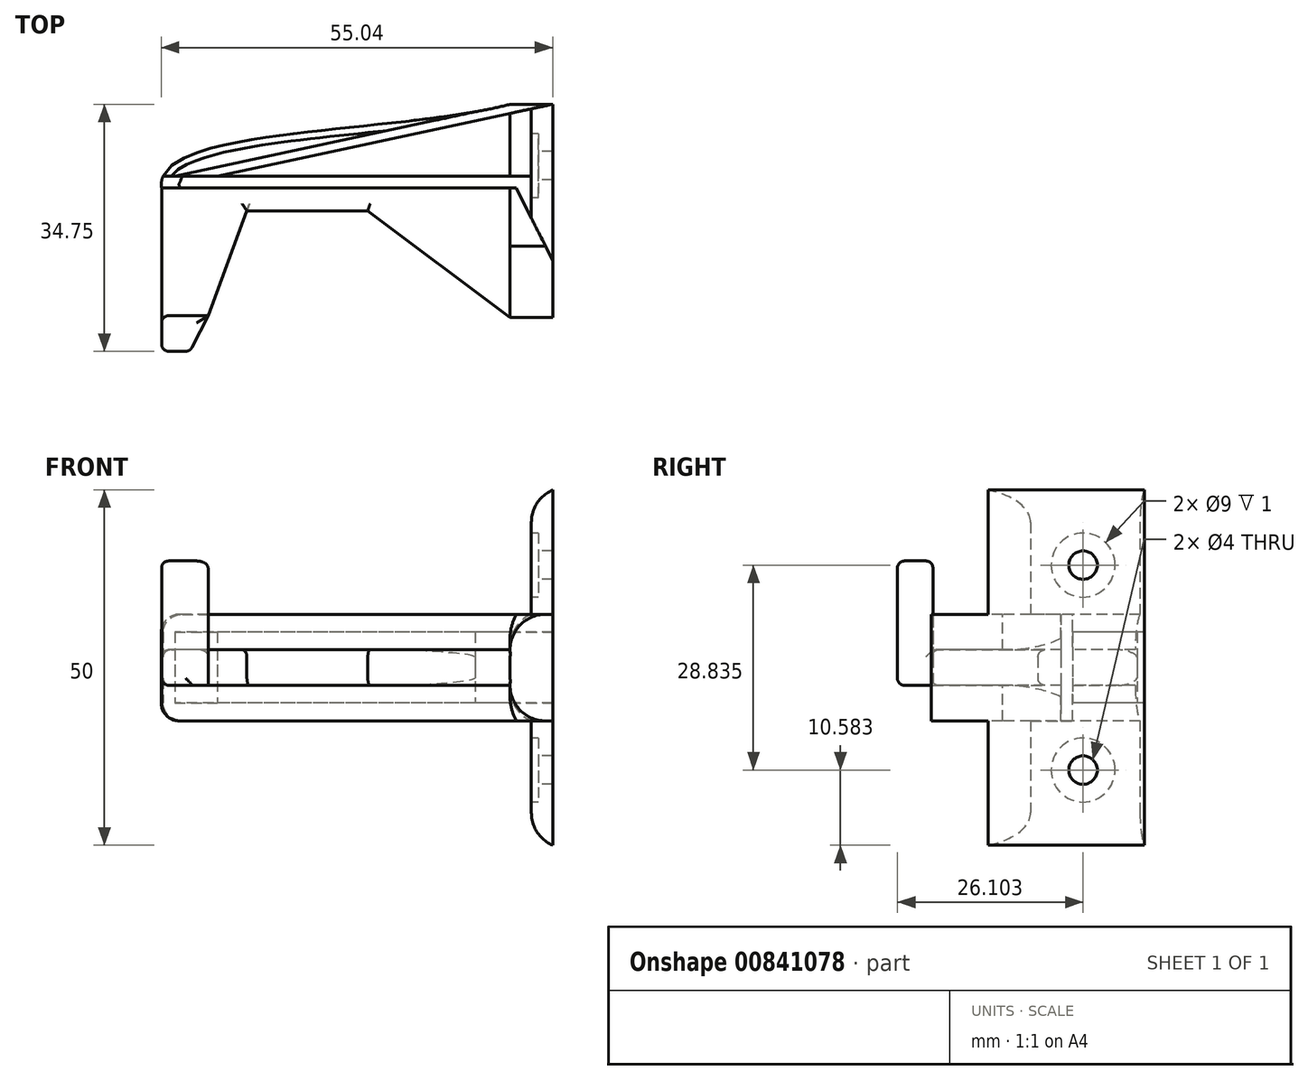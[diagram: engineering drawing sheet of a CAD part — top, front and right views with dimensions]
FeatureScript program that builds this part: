
annotation { "Feature Type Name" : "Feature", "Feature Type Description" : "" }
export const myFeature = defineFeature(function(context is Context, id is Id, definition is map)
    precondition{}
    {
        {
            var Q0;
            Q0=qCreatedBy(makeId("Top.planeOp"),FACE);
            var sketch = newSketch(context, id + "F0", { "sketchPlane" : qUnion([Q0])});
            skLineSegment(sketch, "E0.bottom", {"start": v(24.18, 10.1) * mm, "end": v(30.18, 10.1) * mm});
            skLineSegment(sketch, "E0.top", {"start": v(24.18, -19.9) * mm, "end": v(30.18, -19.9) * mm});
            skLineSegment(sketch, "E0.left", {"start": v(24.18, 10.1) * mm, "end": v(24.18, -19.9) * mm});
            skLineSegment(sketch, "E0.right", {"start": v(30.18, 10.1) * mm, "end": v(30.18, -19.9) * mm});
            skLineSegment(sketch, "E1.right", {"start": v(-18.28, -1.64) * mm, "end": v(-18.28, -4.87) * mm});
            skLineSegment(sketch, "E2.bottom", {"start": v(-18.28, -1.64) * mm, "end": v(-24.82, -1.64) * mm});
            skLineSegment(sketch, "E2.right", {"start": v(-24.82, -1.64) * mm, "end": v(-24.82, -24.64) * mm});
            skLineSegment(sketch, "E3", {"start": v(-24.82, -19.64) * mm, "end": v(-18.28, -19.64) * mm});
            skLineSegment(sketch, "E4", {"start": v(27.18, 10.1) * mm, "end": v(27.18, -19.9) * mm});
            skLineSegment(sketch, "E5", {"start": v(-24.82, -24.64) * mm, "end": v(-20.82, -24.64) * mm});
            skLineSegment(sketch, "E6", {"start": v(-20.82, -24.64) * mm, "end": v(-18.28, -19.64) * mm});
            skLineSegment(sketch, "E7", {"start": v(-18.28, -4.87) * mm, "end": v(-18.28, -19.64) * mm});
            skLineSegment(sketch, "E8", {"start": v(4.18, -4.87) * mm, "end": v(24.18, -19.9) * mm});
            skLineSegment(sketch, "E9", {"start": v(27.18, -5.9) * mm, "end": v(30.18, -11.87) * mm});
            skLineSegment(sketch, "E10", {"start": v(-18.28, -4.87) * mm, "end": v(4.18, -4.87) * mm});
            skFitSpline(sketch, "E11", {"points": [v(24.18, 10.1) * mm, v(-24.82, -1.64) * mm], "startDerivative": vector(-47.95, -12.64) * mm, "endDerivative": vector(4, -26.04) * mm});
            skLineSegment(sketch, "E12", {"start": v(-18.28, -19.64) * mm, "end": v(-12.82, -4.87) * mm});
            skLineSegment(sketch, "E13", {"start": v(-18.28, -1.64) * mm, "end": v(30.18, -1.64) * mm});
            skLineSegment(sketch, "E14", {"start": v(-24.61, 0) * mm, "end": v(30.18, 0) * mm});
            skLineSegment(sketch, "E15", {"start": v(30.18, 10.1) * mm, "end": v(-16.96, 0) * mm});
            skLineSegment(sketch, "E16", {"start": v(24.18, 10.1) * mm, "end": v(-22.96, 0) * mm});
            skSolve(sketch);
        }
        {
            var Q0;
            Q0=makeQuery(id+"F0.imprint","IMPRINT",FACE,{"disambiguationData":[TD([[makeQuery(id+"F0.imprint","IMPRINT",EDGE,{"derivedFrom":sQuery(id+"F0.wireOp",EDGE,"E1.right")}),-1.0]])]});
            var Q1;
            {var subQ2=sQuery(id+"F0.wireOp",EDGE,"E3");Q1=makeQuery(id+"F0.imprint","IMPRINT",FACE,{"disambiguationData":[TD([[makeQuery(id+"F0.imprint","IMPRINT",EDGE,{"derivedFrom":subQ2}),-1.0]])]});}
            var Q2;
            {var subQ2=sQuery(id+"F0.wireOp",EDGE,"E1.right");Q2=makeQuery(id+"F0.imprint","IMPRINT",FACE,{"disambiguationData":[TD([[makeQuery(id+"F0.imprint","IMPRINT",EDGE,{"derivedFrom":subQ2}),1.0]])]});}
            var Q3;
            {var subQ0=sQuery(id+"F0.wireOp",EDGE,"E15");var subQ1=sQuery(id+"F0.wireOp",EDGE,"E0.left");var subQ2=makeQuery(id+"F0.imprint","INTERSECT",VERTEX,{"derivedFrom":[subQ1,subQ0]});Q3=makeQuery(id+"F0.imprint","IMPRINT",FACE,{"disambiguationData":[TD([[makeQuery(id+"F0.imprint","IMPRINT",EDGE,{"disambiguationData":[TD([[subQ2,-1.0]])],"derivedFrom":subQ1}),-1.0]])]});}
            var Q4;
            {var subQ0=sQuery(id+"F0.wireOp",EDGE,"E11");var subQ5=sQuery(id+"F0.wireOp",EDGE,"E14");var subQ6=makeQuery(id+"F0.imprint","INTERSECT",VERTEX,{"derivedFrom":[subQ0,subQ5]});Q4=makeQuery(id+"F0.imprint","IMPRINT",FACE,{"disambiguationData":[TD([[makeQuery(id+"F0.imprint","IMPRINT",EDGE,{"disambiguationData":[TD([[subQ6,-1.0]])],"derivedFrom":subQ5}),1.0]])]});}
            var Q5;
            {var subQ0=sQuery(id+"F0.wireOp",EDGE,"E7");Q5=makeQuery(id+"F0.imprint","IMPRINT",FACE,{"disambiguationData":[TD([[makeQuery(id+"F0.imprint","IMPRINT",EDGE,{"derivedFrom":subQ0}),1.0]])]});}
            extrude(context, id + "F1", {"entities" : qUnion([Q0, Q1, Q2, Q3, Q4, Q5]), "endBound" : BoundingType.SYMMETRIC, "depth" : 5 * mm, "offsetDistance" : 25 * mm});
        }
        {
            var Q0;
            {var subQ3=sQuery(id+"F0.wireOp",EDGE,"E1.left");Q0=makeQuery(id+"F0.imprint","IMPRINT",FACE,{"disambiguationData":[TD([[makeQuery(id+"F0.imprint","IMPRINT",EDGE,{"derivedFrom":subQ3}),1.0]])]});}
            var Q1;
            {var subQ5=sQuery(id+"F0.wireOp",EDGE,"E9");Q1=makeQuery(id+"F0.imprint","IMPRINT",FACE,{"disambiguationData":[TD([[makeQuery(id+"F0.imprint","IMPRINT",EDGE,{"derivedFrom":subQ5}),-1.0]])]});}
            var Q2;
            {var subQ0=sQuery(id+"F0.wireOp",EDGE,"E4");var subQ1=makeQuery(id+"F0.imprint","INTERSECT",VERTEX,{"derivedFrom":[subQ0,sQuery(id+"F0.wireOp",EDGE,"E9")]});Q2=makeQuery(id+"F0.imprint","IMPRINT",FACE,{"disambiguationData":[TD([[makeQuery(id+"F0.imprint","IMPRINT",EDGE,{"disambiguationData":[TD([[subQ1,1.0]])],"derivedFrom":subQ0}),-1.0]])]});}
            var Q3;
            {var subQ0=sQuery(id+"F0.wireOp",EDGE,"E14");var subQ1=sQuery(id+"F0.wireOp",EDGE,"E0.left");var subQ2=makeQuery(id+"F0.imprint","INTERSECT",VERTEX,{"derivedFrom":[subQ1,subQ0]});Q3=makeQuery(id+"F0.imprint","IMPRINT",FACE,{"disambiguationData":[TD([[makeQuery(id+"F0.imprint","IMPRINT",EDGE,{"disambiguationData":[TD([[subQ2,-1.0]])],"derivedFrom":subQ1}),1.0]])]});}
            var Q4;
            {var subQ0=sQuery(id+"F0.wireOp",EDGE,"E15");var subQ1=sQuery(id+"F0.wireOp",EDGE,"E0.left");var subQ2=makeQuery(id+"F0.imprint","INTERSECT",VERTEX,{"derivedFrom":[subQ1,subQ0]});Q4=makeQuery(id+"F0.imprint","IMPRINT",FACE,{"disambiguationData":[TD([[makeQuery(id+"F0.imprint","IMPRINT",EDGE,{"disambiguationData":[TD([[subQ2,-1.0]])],"derivedFrom":subQ1}),1.0]])]});}
            var Q5;
            {var subQ1=sQuery(id+"F0.wireOp",EDGE,"E2.bottom");Q5=makeQuery(id+"F0.imprint","IMPRINT",FACE,{"disambiguationData":[TD([[makeQuery(id+"F0.imprint","IMPRINT",EDGE,{"derivedFrom":subQ1}),-1.0]])]});}
            extrude(context, id + "F2", {"entities" : qUnion([Q0, Q1, Q2, Q3, Q4, Q5]), "operationType" : NewBodyOperationType.ADD, "endBound" : BoundingType.SYMMETRIC, "depth" : 15 * mm, "offsetDistance" : 25 * mm});
        }
        {
            var Q0;
            {var subQ5=sQuery(id+"F0.wireOp",EDGE,"E9");Q0=makeQuery(id+"F0.imprint","IMPRINT",FACE,{"disambiguationData":[TD([[makeQuery(id+"F0.imprint","IMPRINT",EDGE,{"derivedFrom":subQ5}),1.0]])]});}
            var Q1;
            {var subQ0=sQuery(id+"F0.wireOp",EDGE,"E15");var subQ5=sQuery(id+"F0.wireOp",EDGE,"E4");var subQ6=makeQuery(id+"F0.imprint","INTERSECT",VERTEX,{"derivedFrom":[subQ5,subQ0]});Q1=makeQuery(id+"F0.imprint","IMPRINT",FACE,{"disambiguationData":[TD([[makeQuery(id+"F0.imprint","IMPRINT",EDGE,{"disambiguationData":[TD([[subQ6,-1.0]])],"derivedFrom":subQ5}),1.0]])]});}
            var Q2;
            {var subQ0=sQuery(id+"F0.wireOp",EDGE,"E13");var subQ1=sQuery(id+"F0.wireOp",EDGE,"E0.right");var subQ2=makeQuery(id+"F0.imprint","INTERSECT",VERTEX,{"derivedFrom":[subQ1,subQ0]});Q2=makeQuery(id+"F0.imprint","IMPRINT",FACE,{"disambiguationData":[TD([[makeQuery(id+"F0.imprint","IMPRINT",EDGE,{"disambiguationData":[TD([[subQ2,1.0]])],"derivedFrom":subQ1}),-1.0]])]});}
            extrude(context, id + "F3", {"entities" : qUnion([Q0, Q1, Q2]), "operationType" : NewBodyOperationType.ADD, "endBound" : BoundingType.SYMMETRIC, "depth" : 50 * mm, "offsetDistance" : 25 * mm});
        }
        {
            var Q0;
            {var subQ2=sQuery(id+"F0.wireOp",EDGE,"E3");Q0=makeQuery(id+"F0.imprint","IMPRINT",FACE,{"disambiguationData":[TD([[makeQuery(id+"F0.imprint","IMPRINT",EDGE,{"derivedFrom":subQ2}),-1.0]])]});}
            var Q1;
            Q1=makeQuery(id+"F1.opExtrude","SWEPT_BODY",BODY,{"disambiguationData":[OSD([sQuery(id+"F0.wireOp",EDGE,"E0.left"),sQuery(id+"F0.wireOp",EDGE,"E1.left"),sQuery(id+"F0.wireOp",EDGE,"E2.right"),sQuery(id+"F0.wireOp",EDGE,"E3"),sQuery(id+"F0.wireOp",EDGE,"E7"),sQuery(id+"F0.wireOp",EDGE,"2QqUce5b-Nnzw-vXuS-maCt-9JAGvlBEQTfu"),sQuery(id+"F0.wireOp",EDGE,"nEMrKmD4-wK41-gVLx-OtnK-8CKE1vO8Bu5v"),sQuery(id+"F0.wireOp",EDGE,"E8"),sQuery(id+"F0.wireOp",EDGE,"b5387394-8ce0-4926-b781-dd25e73307f8")])]});
            extrude(context, id + "F4", {"entities" : qUnion([Q0]), "operationType" : NewBodyOperationType.ADD, "depth" : 15 * mm, "endBoundEntityBody" : qUnion([Q1]), "offsetDistance" : 25 * mm});
        }
        {
            var Q0;
            {var subQ2=sQuery(id+"F0.wireOp",EDGE,"E3");Q0=makeQuery(id+"F0.imprint","IMPRINT",FACE,{"disambiguationData":[TD([[makeQuery(id+"F0.imprint","IMPRINT",EDGE,{"derivedFrom":subQ2}),-1.0]])]});}
            extrude(context, id + "F5", {"entities" : qUnion([Q0]), "operationType" : NewBodyOperationType.ADD, "endBound" : BoundingType.SYMMETRIC, "depth" : 5 * mm, "offsetDistance" : 25 * mm});
        }
        {
            var Q0;
            {var subQ0=sQuery(id+"F0.wireOp",EDGE,"E15");var subQ1=sQuery(id+"F0.wireOp",EDGE,"E14");var subQ2=makeQuery(id+"F0.imprint","INTERSECT",VERTEX,{"derivedFrom":[subQ1,subQ0]});Q0=makeQuery(id+"F0.imprint","IMPRINT",FACE,{"disambiguationData":[TD([[makeQuery(id+"F0.imprint","IMPRINT",EDGE,{"disambiguationData":[TD([[subQ2,1.0]])],"derivedFrom":subQ1}),1.0]])]});}
            var Q1;
            {var subQ1=sQuery(id+"F0.wireOp",EDGE,"E0.bottom");var subQ3=sQuery(id+"F0.wireOp",EDGE,"E4");var subQ4=makeQuery(id+"F0.imprint","INTERSECT",VERTEX,{"derivedFrom":[subQ1,subQ3]});Q1=makeQuery(id+"F0.imprint","IMPRINT",FACE,{"disambiguationData":[TD([[makeQuery(id+"F0.imprint","IMPRINT",EDGE,{"disambiguationData":[TD([[subQ4,-1.0]])],"derivedFrom":subQ3}),-1.0]])]});}
            var Q2;
            {var subQ1=sQuery(id+"F0.wireOp",EDGE,"E0.bottom");var subQ3=sQuery(id+"F0.wireOp",EDGE,"E4");var subQ4=makeQuery(id+"F0.imprint","INTERSECT",VERTEX,{"derivedFrom":[subQ1,subQ3]});Q2=makeQuery(id+"F0.imprint","IMPRINT",FACE,{"disambiguationData":[TD([[makeQuery(id+"F0.imprint","IMPRINT",EDGE,{"disambiguationData":[TD([[subQ4,-1.0]])],"derivedFrom":subQ3}),1.0]])]});}
            extrude(context, id + "F6", {"entities" : qUnion([Q0, Q1, Q2]), "endBound" : BoundingType.SYMMETRIC, "depth" : 10 * mm, "offsetDistance" : 25 * mm});
        }
        {
            var Q0;
            {var subQ0=sQuery(id+"F0.wireOp",EDGE,"E0.left");Q0=makeQuery(id+"F2.opExtrude","CAP_EDGE",EDGE,{"disambiguationData":[OSD([subQ0]),TDD([makeQuery(id+"F0.imprint","IMPRINT",EDGE,{"disambiguationData":[TD([[makeQuery(id+"F0.imprint","INTERSECT",VERTEX,{"derivedFrom":[subQ0,sQuery(id+"F0.wireOp",EDGE,"E15")]}),-1.0]])],"derivedFrom":subQ0})])],"isStart":false});}
            var Q1;
            {var subQ0=sQuery(id+"F0.wireOp",EDGE,"E0.left");Q1=makeQuery(id+"F2.opExtrude","CAP_EDGE",EDGE,{"disambiguationData":[OSD([subQ0]),TDD([makeQuery(id+"F0.imprint","IMPRINT",EDGE,{"disambiguationData":[TD([[makeQuery(id+"F0.imprint","INTERSECT",VERTEX,{"derivedFrom":[subQ0,sQuery(id+"F0.wireOp",EDGE,"E13")]}),-1.0]])],"derivedFrom":subQ0})])],"isStart":false});}
            var Q2;
            Q2=makeQuery(id+"F3.opExtrude","CAP_EDGE",EDGE,{"disambiguationData":[OSD([sQuery(id+"F0.wireOp",EDGE,"E4")])],"isStart":false});
            var Q3;
            {var subQ0=sQuery(id+"F0.wireOp",EDGE,"E0.left");Q3=makeQuery(id+"F2.opExtrude","CAP_EDGE",EDGE,{"disambiguationData":[OSD([subQ0]),TDD([makeQuery(id+"F0.imprint","IMPRINT",EDGE,{"disambiguationData":[TD([[makeQuery(id+"F0.imprint","INTERSECT",VERTEX,{"derivedFrom":[subQ0,sQuery(id+"F0.wireOp",EDGE,"E13")]}),-1.0]])],"derivedFrom":subQ0})])],"isStart":true});}
            var Q4;
            {var subQ0=sQuery(id+"F0.wireOp",EDGE,"E0.left");Q4=makeQuery(id+"F2.opExtrude","CAP_EDGE",EDGE,{"disambiguationData":[OSD([subQ0]),TDD([makeQuery(id+"F0.imprint","IMPRINT",EDGE,{"disambiguationData":[TD([[makeQuery(id+"F0.imprint","INTERSECT",VERTEX,{"derivedFrom":[subQ0,sQuery(id+"F0.wireOp",EDGE,"E15")]}),-1.0]])],"derivedFrom":subQ0})])],"isStart":true});}
            var Q5;
            Q5=makeQuery(id+"F3.opExtrude","CAP_EDGE",EDGE,{"disambiguationData":[OSD([sQuery(id+"F0.wireOp",EDGE,"E4")])],"isStart":true});
            fillet(context, id + "F7", {"entities" : qUnion([Q0, Q1, Q2, Q3, Q4, Q5]), "radius" : 5 * mm, "tangentPropagation" : true, "allowEdgeOverflow" : false});
        }
        {
            var Q0;
            Q0=makeQuery(id+"F4.opExtrude","SWEPT_EDGE",EDGE,{"disambiguationData":[OSD([sQuery(id+"F0.wireOp",EDGE,"E2.right"),sQuery(id+"F0.wireOp",EDGE,"E3")])]});
            var Q1;
            {var subQ0=sQuery(id+"F0.wireOp",EDGE,"E6");var subQ1=sQuery(id+"F0.wireOp",EDGE,"E5");Q1=makeQuery(id+"F4.boolean.opBoolean","MERGE",EDGE,{"derivedFrom":[makeQuery(id+"F1.opExtrude","SWEPT_EDGE",EDGE,{"disambiguationData":[OSD([subQ1,subQ0])]}),makeQuery(id+"F4.opExtrude","SWEPT_EDGE",EDGE,{"disambiguationData":[OSD([subQ1,subQ0])]})]});}
            var Q2;
            {var subQ0=sQuery(id+"F0.wireOp",EDGE,"E5");var subQ1=sQuery(id+"F0.wireOp",EDGE,"E2.right");Q2=makeQuery(id+"F4.boolean.opBoolean","MERGE",EDGE,{"derivedFrom":[makeQuery(id+"F1.opExtrude","SWEPT_EDGE",EDGE,{"disambiguationData":[OSD([subQ1,subQ0])]}),makeQuery(id+"F4.opExtrude","SWEPT_EDGE",EDGE,{"disambiguationData":[OSD([subQ1,subQ0])]})]});}
            var Q3;
            Q3=makeQuery(id+"F1.opExtrude","CAP_EDGE",EDGE,{"disambiguationData":[OSD([sQuery(id+"F0.wireOp",EDGE,"E2.right")])],"isStart":false});
            var Q4;
            Q4=makeQuery(id+"F1.opExtrude","CAP_EDGE",EDGE,{"disambiguationData":[OSD([sQuery(id+"F0.wireOp",EDGE,"E10")])],"isStart":false});
            var Q5;
            Q5=makeQuery(id+"F1.opExtrude","CAP_EDGE",EDGE,{"disambiguationData":[OSD([sQuery(id+"F0.wireOp",EDGE,"E12")])],"isStart":false});
            var Q6;
            Q6=makeQuery(id+"F4.opExtrude","CAP_EDGE",EDGE,{"disambiguationData":[OSD([sQuery(id+"F0.wireOp",EDGE,"E5")])],"isStart":false});
            var Q7;
            Q7=makeQuery(id+"F4.opExtrude","CAP_EDGE",EDGE,{"disambiguationData":[OSD([sQuery(id+"F0.wireOp",EDGE,"E6")])],"isStart":false});
            var Q8;
            Q8=makeQuery(id+"F4.opExtrude","CAP_EDGE",EDGE,{"disambiguationData":[OSD([sQuery(id+"F0.wireOp",EDGE,"E3")])],"isStart":false});
            var Q9;
            Q9=makeQuery(id+"F4.opExtrude","CAP_EDGE",EDGE,{"disambiguationData":[OSD([sQuery(id+"F0.wireOp",EDGE,"E2.right")])],"isStart":false});
            var Q10;
            Q10=makeQuery(id+"F1.opExtrude","CAP_EDGE",EDGE,{"disambiguationData":[OSD([sQuery(id+"F0.wireOp",EDGE,"E8")])],"isStart":false});
            var Q11;
            Q11=makeQuery(id+"F1.opExtrude","CAP_EDGE",EDGE,{"disambiguationData":[OSD([sQuery(id+"F0.wireOp",EDGE,"E5")])],"isStart":true});
            var Q12;
            Q12=makeQuery(id+"F1.opExtrude","CAP_EDGE",EDGE,{"disambiguationData":[OSD([sQuery(id+"F0.wireOp",EDGE,"E10")])],"isStart":true});
            var Q13;
            Q13=makeQuery(id+"F1.opExtrude","CAP_EDGE",EDGE,{"disambiguationData":[OSD([sQuery(id+"F0.wireOp",EDGE,"E8")])],"isStart":true});
            var Q14;
            Q14=makeQuery(id+"F1.opExtrude","CAP_EDGE",EDGE,{"disambiguationData":[OSD([sQuery(id+"F0.wireOp",EDGE,"E2.right")])],"isStart":true});
            var Q15;
            Q15=makeQuery(id+"F1.opExtrude","CAP_EDGE",EDGE,{"disambiguationData":[OSD([sQuery(id+"F0.wireOp",EDGE,"E11")])],"isStart":false});
            var Q16;
            Q16=makeQuery(id+"F1.opExtrude","CAP_EDGE",EDGE,{"disambiguationData":[OSD([sQuery(id+"F0.wireOp",EDGE,"E11")])],"isStart":true});
            fillet(context, id + "F8", {"entities" : qUnion([Q0, Q1, Q2, Q3, Q4, Q5, Q6, Q7, Q8, Q9, Q10, Q11, Q12, Q13, Q14, Q15, Q16]), "radius" : 1 * mm, "tangentPropagation" : true, "allowEdgeOverflow" : false});
        }
        {
            var Q0;
            {var subQ0=sQuery(id+"F0.wireOp",EDGE,"E15");var subQ1=sQuery(id+"F0.wireOp",EDGE,"E9");var subQ2=sQuery(id+"F0.wireOp",EDGE,"E4");var subQ3=sQuery(id+"F0.wireOp",EDGE,"E0.right");Q0=makeQuery(id+"F3.boolean.opBoolean","SPLIT",FACE,{"disambiguationData":[TD([makeQuery(id+"F3.opExtrude","CAP_FACE",FACE,{"disambiguationData":[OSD([subQ3,subQ2,subQ1,subQ0])],"isStart":false})])],"derivedFrom":makeQuery(id+"F3.opExtrude","SWEPT_FACE",FACE,{"disambiguationData":[OSD([subQ2])]})});}
            var sketch = newSketch(context, id + "F9", { "sketchPlane" : qUnion([Q0])});
            skCircle(sketch, "E17", {"center": v(-1.46, 14.42) * mm, "radius": 4.5 * mm});
            skCircle(sketch, "E18", {"center": v(-1.46, -14.42) * mm, "radius": 4.5 * mm});
            skCircle(sketch, "E19", {"center": v(-1.46, 14.42) * mm, "radius": 2 * mm});
            skCircle(sketch, "E20", {"center": v(-1.46, -14.42) * mm, "radius": 2 * mm});
            skSolve(sketch);
        }
        {
            var Q0;
            Q0=makeQuery(id+"F2.opExtrude","CAP_EDGE",EDGE,{"disambiguationData":[OSD([sQuery(id+"F0.wireOp",EDGE,"E11")])],"isStart":false});
            var Q1;
            Q1=makeQuery(id+"F2.opExtrude","CAP_EDGE",EDGE,{"disambiguationData":[OSD([sQuery(id+"F0.wireOp",EDGE,"E11")])],"isStart":true});
            fillet(context, id + "F10", {"entities" : qUnion([Q0, Q1]), "radius" : 2.5 * mm, "tangentPropagation" : true, "allowEdgeOverflow" : false});
        }
        {
            var Q0;
            Q0 = qSketchRegion(id + "F9", true);
            extrude(context, id + "F11", {"entities" : qUnion([Q0]), "operationType" : NewBodyOperationType.REMOVE, "oppositeDirection" : true, "depth" : 1 * mm, "offsetDistance" : 25 * mm});
        }
        {
            var Q0;
            {var subQ0=sQuery(id+"F0.wireOp",EDGE,"E15");var subQ1=sQuery(id+"F0.wireOp",EDGE,"E9");var subQ2=sQuery(id+"F0.wireOp",EDGE,"E4");var subQ3=sQuery(id+"F0.wireOp",EDGE,"E0.right");Q0=makeQuery(id+"F11.boolean.opBoolean","SPLIT",FACE,{"disambiguationData":[TD([makeQuery(id+"F11.opExtrude","SWEPT_FACE",FACE,{"disambiguationData":[OSD([sQuery(id+"F9.wireOp",EDGE,"E20")])]})])],"derivedFrom":makeQuery(id+"F3.boolean.opBoolean","SPLIT",FACE,{"disambiguationData":[TD([makeQuery(id+"F3.opExtrude","CAP_FACE",FACE,{"disambiguationData":[OSD([subQ3,subQ2,subQ1,subQ0])],"isStart":true})])],"derivedFrom":makeQuery(id+"F3.opExtrude","SWEPT_FACE",FACE,{"disambiguationData":[OSD([subQ2])]})})});}
            var Q1;
            {var subQ0=sQuery(id+"F0.wireOp",EDGE,"E15");var subQ1=sQuery(id+"F0.wireOp",EDGE,"E9");var subQ2=sQuery(id+"F0.wireOp",EDGE,"E4");var subQ3=sQuery(id+"F0.wireOp",EDGE,"E0.right");Q1=makeQuery(id+"F11.boolean.opBoolean","SPLIT",FACE,{"disambiguationData":[TD([makeQuery(id+"F11.opExtrude","SWEPT_FACE",FACE,{"disambiguationData":[OSD([sQuery(id+"F9.wireOp",EDGE,"E19")])]})])],"derivedFrom":makeQuery(id+"F3.boolean.opBoolean","SPLIT",FACE,{"disambiguationData":[TD([makeQuery(id+"F3.opExtrude","CAP_FACE",FACE,{"disambiguationData":[OSD([subQ3,subQ2,subQ1,subQ0])],"isStart":false})])],"derivedFrom":makeQuery(id+"F3.opExtrude","SWEPT_FACE",FACE,{"disambiguationData":[OSD([subQ2])]})})});}
            extrude(context, id + "F12", {"entities" : qUnion([Q0, Q1]), "operationType" : NewBodyOperationType.REMOVE, "oppositeDirection" : true, "depth" : 25 * mm, "offsetDistance" : 25 * mm});
        }
    });
